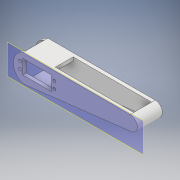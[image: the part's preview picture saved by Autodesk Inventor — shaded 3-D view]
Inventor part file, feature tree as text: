
AUTODESK INVENTOR PART (.ipt)
format: ipt  version: 2018 (Build 220112000, 112)  size: 151,040 bytes
history: native  units: mm
features: other x3, plane x1, mirror x1
ambient origin geometry x8: Origin, YZ Plane, XZ Plane, XY Plane, X Axis, Y Axis, Z Axis, Center Point
bodies: Solid1 (feature_tree)
feature tree (5):
  other  "Tibia"
  plane  "Work Plane1"
  mirror  "Mirror1"
  other  "Solid1::Tibia"
  other  "TaggingFeature1"
